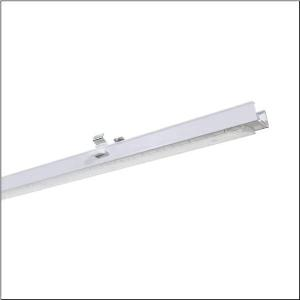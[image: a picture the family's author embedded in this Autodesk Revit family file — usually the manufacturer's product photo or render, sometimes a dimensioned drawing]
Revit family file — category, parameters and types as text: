
# Revit family: trunking_flex_31_51re12ma66b
name_source: partatom
category: Lighting Fixtures
units: mm (PartAtom-declared; Revit-internal decimal feet)

## family parameters
Cut with Voids When Loaded = No
Host = Face
Light Source = No
Part Type = Normal
Room Calculation Point = No
Round Connector Dimension = Use Diameter
Shared = No

## types (1)
- --- (1 x LED, 6400 lm, 40 W, 6500K)
    Apparent Load = 40 VA
    CIE Flux Codes = 65 91 98 99 100
    Color Rendering = 80
    Color Temperature = 6500K
    Default Elevation = 1800 mm
    Description = Trunking Flex 31, luminaire insert, of extruded aluminium section, coated, traffic white (RAL 9016), length: 1.172mm, width: 91mm, height: 53mm, LED rated luminous flux: 6.400lm, light colour: 865, control gear: ON/OFF Multilumen, with system connector: socket, mains connection: 220..240V, AC, 50/60Hz, rated input power: 40W, luminous flux adjustable on luminaire in four steps (3420/4540/5580/6630lm), connected load according to luminous flux setting (20/26/33/40W), primary light control with lens, of plastic, primary optical cover: cover, of PMMA, light emission: direct distribution, protection rating (complete): IP20, insulation class (complete): insulation class I (protective earthing), certification: CE, UKCA, impact resistance: IK02, permissible ambient temperature for indoor applications: -20..+40°C, packaging unit: 1 piece
    Height = 58 mm
    Lamp = 1 x LED
    Lamp Light Flux = 6400 lm
    Lamp Power = 40 W
    Lamp count = 1
    Length = 1172 mm
    Luminous efficacy = 160 lm/W
    Manufacturer = Siteco
    ModVariant = No
    Model = 51RE12MA66B
    Mounting Place = Ceiling
    Mounting Type = Pendant
    Number of Poles = 1
    OnlyDefault = Yes
    Power Factor = 1
    Product Name = Trunking Flex 31
    Product group = luminaire insert
    ProductGroupID = 901
    Protection Class = Protection class I
    Protection Degree = IP 20
    RLX_Detail_Level = 1
    RLX_Emergency_Light_Flux = 0 lm
    RLX_Emergency_Type = 0
    RLX_Emergency_Type_DB = No
    RlxData = <blob elided: 19953 chars, md5=fec7bf2e>
    Socket = socket
    Standby Power = 0 W
    System Light Flux = 6400 lm
    System Power = 40 W
    Type Comments = factory setting: luminous flux: 100 % | (ON | ON) | 300 mA
    Type Image = l_1266702.jpg
    URL = http://relux.com
    VarID = @adj_018673
    Voltage = 0 V
    Weight = 0.00 kg
    Width = 65 mm

## geometry (parser evidence)
native form markers: Blend x4, Sweep x13
no freeform markers — native parametric forms only
